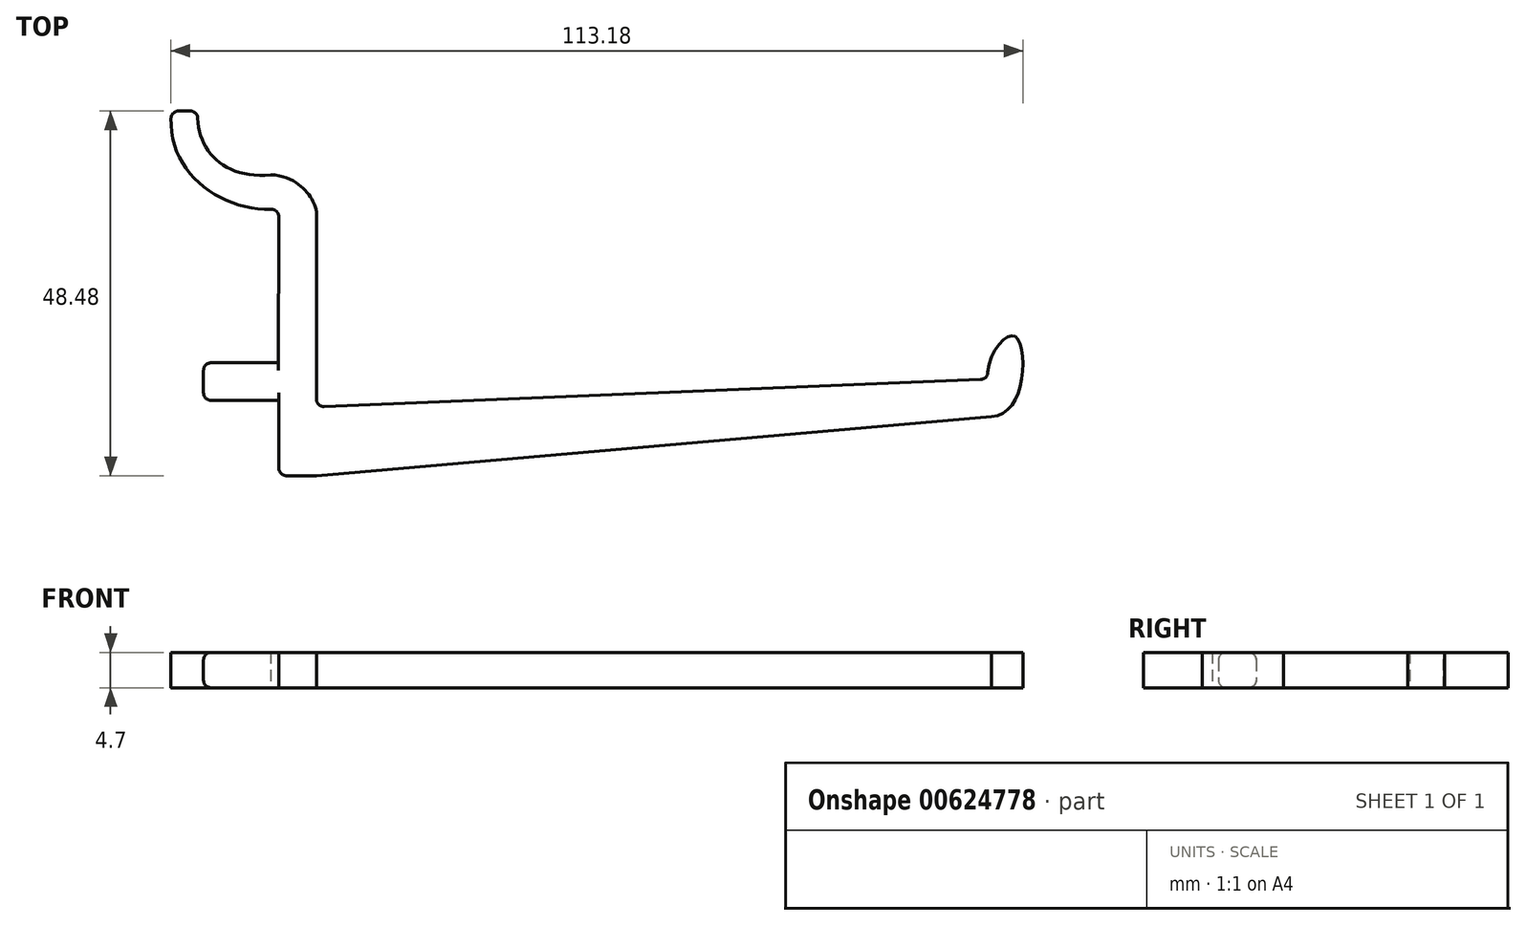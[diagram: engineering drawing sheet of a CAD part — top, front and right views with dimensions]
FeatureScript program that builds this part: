
annotation { "Feature Type Name" : "Feature", "Feature Type Description" : "" }
export const myFeature = defineFeature(function(context is Context, id is Id, definition is map)
    precondition{}
    {
        {
            var Q0;
            Q0=qCreatedBy(makeId("Top.planeOp"),FACE);
            var sketch = newSketch(context, id + "F0", { "sketchPlane" : qUnion([Q0])});
            skLineSegment(sketch, "E0", {"start": v(-15.83, 26.17) * mm, "end": v(-12.33, 26.17) * mm});
            skFitSpline(sketch, "E1", {"points": [v(-12.33, 26.17) * mm, v(-2.65, 17.69) * mm], "startDerivative": vector(-1.06, -15.17) * mm, "endDerivative": vector(19.05, 1.96) * mm});
            skFitSpline(sketch, "E2", {"points": [v(-2.65, 17.69) * mm, v(3.42, 12.83) * mm], "startDerivative": vector(13.6, -0.54) * mm, "endDerivative": vector(0.17, -2.2) * mm});
            skFitSpline(sketch, "E3", {"points": [v(-15.83, 26.17) * mm, v(-1.58, 13.19) * mm], "startDerivative": vector(-2.9, -24.56) * mm, "endDerivative": vector(21.9, 2.52) * mm});
            skLineSegment(sketch, "E4", {"start": v(3.42, -22.31) * mm, "end": v(-1.58, -22.31) * mm});
            skLineSegment(sketch, "E5", {"start": v(-1.58, -22.31) * mm, "end": v(-1.58, -12.31) * mm});
            skLineSegment(sketch, "E6", {"start": v(-1.58, -12.31) * mm, "end": v(-11.58, -12.31) * mm});
            skLineSegment(sketch, "E7", {"start": v(-11.58, -12.31) * mm, "end": v(-11.58, -7.31) * mm});
            skLineSegment(sketch, "E8", {"start": v(-11.58, -7.31) * mm, "end": v(-1.65, -7.31) * mm});
            skLineSegment(sketch, "E9", {"start": v(-1.65, -7.31) * mm, "end": v(-1.58, 13.19) * mm});
            skLineSegment(sketch, "E10", {"start": v(3.42, -22.31) * mm, "end": v(93.07, -14.47) * mm});
            skLineSegment(sketch, "E11", {"start": v(93.07, -14.47) * mm, "end": v(92.64, -9.49) * mm});
            skLineSegment(sketch, "E12", {"start": v(92.64, -9.49) * mm, "end": v(3.42, -13.17) * mm});
            skFitSpline(sketch, "E13", {"points": [v(92.64, -9.49) * mm, v(95.94, -3.71) * mm, v(97.11, -9.41) * mm, v(93.07, -14.47) * mm], "startDerivative": vector(-2.9, 25.83) * mm, "endDerivative": vector(-21.3, -1.07) * mm});
            skLineSegment(sketch, "E14", {"start": v(3.42, 12.83) * mm, "end": v(3.42, -13.17) * mm});
            skSolve(sketch);
        }
        {
            var Q0;
            Q0 = qSketchRegion(id + "F0", true);
            extrude(context, id + "F1", {"entities" : qUnion([Q0]), "depth" : 4.7 * mm, "offsetDistance" : 25 * mm});
        }
        {
            var Q0;
            Q0=makeQuery(id+"F1.opExtrude","CAP_EDGE",EDGE,{"disambiguationData":[OSD([sQuery(id+"F0.wireOp",EDGE,"E8")])],"isStart":false});
            var Q1;
            Q1=makeQuery(id+"F1.opExtrude","CAP_EDGE",EDGE,{"disambiguationData":[OSD([sQuery(id+"F0.wireOp",EDGE,"E6")])],"isStart":false});
            var Q2;
            Q2=makeQuery(id+"F1.opExtrude","CAP_EDGE",EDGE,{"disambiguationData":[OSD([sQuery(id+"F0.wireOp",EDGE,"E8")])],"isStart":true});
            var Q3;
            Q3=makeQuery(id+"F1.opExtrude","CAP_EDGE",EDGE,{"disambiguationData":[OSD([sQuery(id+"F0.wireOp",EDGE,"E6")])],"isStart":true});
            var Q4;
            Q4=makeQuery(id+"F1.opExtrude","SWEPT_FACE",FACE,{"disambiguationData":[OSD([sQuery(id+"F0.wireOp",EDGE,"E7")])]});
            var Q5;
            Q5=makeQuery(id+"F1.opExtrude","SWEPT_EDGE",EDGE,{"disambiguationData":[OSD([sQuery(id+"F0.wireOp",EDGE,"E0"),sQuery(id+"F0.wireOp",EDGE,"E3")])]});
            var Q6;
            Q6=makeQuery(id+"F1.opExtrude","SWEPT_EDGE",EDGE,{"disambiguationData":[OSD([sQuery(id+"F0.wireOp",EDGE,"E0"),sQuery(id+"F0.wireOp",EDGE,"E1")])]});
            var Q7;
            Q7=makeQuery(id+"F1.opExtrude","SWEPT_EDGE",EDGE,{"disambiguationData":[OSD([sQuery(id+"F0.wireOp",EDGE,"E3"),sQuery(id+"F0.wireOp",EDGE,"E9")])]});
            var Q8;
            Q8=makeQuery(id+"F1.opExtrude","SWEPT_EDGE",EDGE,{"disambiguationData":[OSD([sQuery(id+"F0.wireOp",EDGE,"E4"),sQuery(id+"F0.wireOp",EDGE,"E5")])]});
            var Q9;
            Q9=makeQuery(id+"F1.opExtrude","SWEPT_EDGE",EDGE,{"disambiguationData":[OSD([sQuery(id+"F0.wireOp",EDGE,"5cbcd245-8ede-4d35-b9b0-b6ac71820376"),sQuery(id+"F0.wireOp",EDGE,"E12")])]});
            var Q10;
            Q10=makeQuery(id+"F1.opExtrude","SWEPT_EDGE",EDGE,{"disambiguationData":[OSD([sQuery(id+"F0.wireOp",EDGE,"E11"),sQuery(id+"F0.wireOp",EDGE,"E12"),sQuery(id+"F0.wireOp",EDGE,"E13")])]});
            fillet(context, id + "F2", {"entities" : qUnion([Q0, Q1, Q2, Q3, Q4, Q5, Q6, Q7, Q8, Q9, Q10]), "radius" : 1 * mm, "tangentPropagation" : true, "allowEdgeOverflow" : false});
        }
    });
